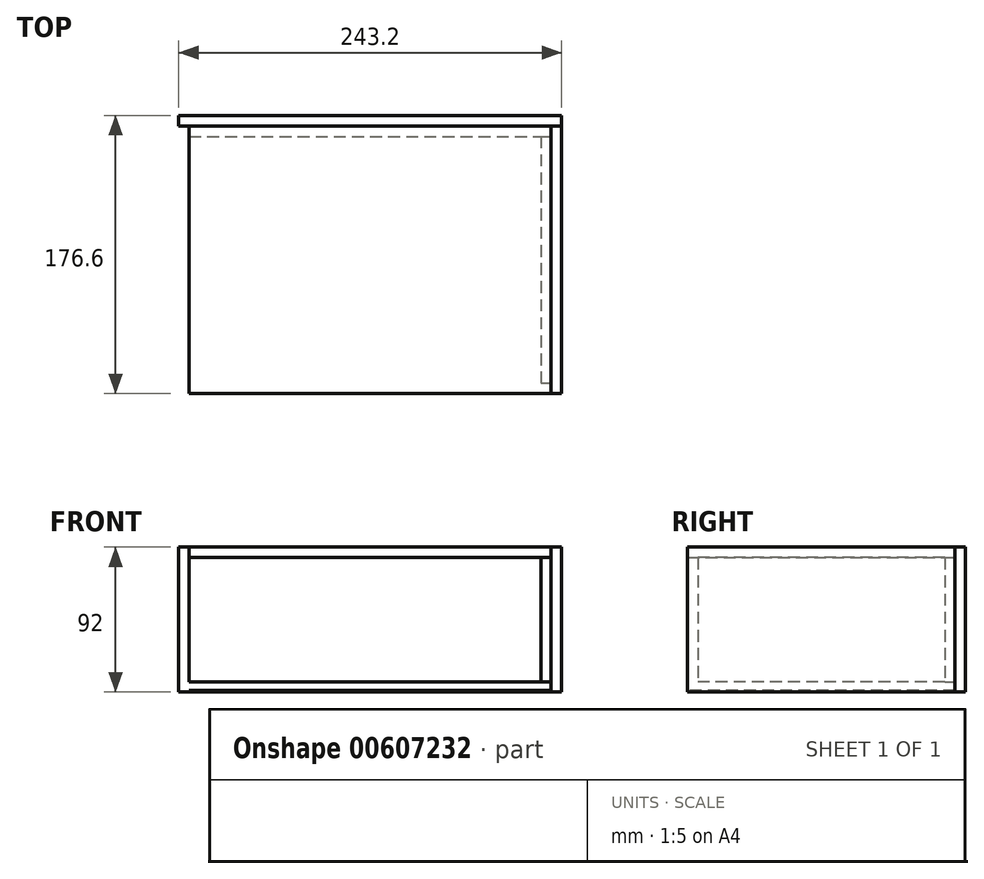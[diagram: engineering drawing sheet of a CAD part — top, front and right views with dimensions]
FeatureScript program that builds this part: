
annotation { "Feature Type Name" : "Feature", "Feature Type Description" : "" }
export const myFeature = defineFeature(function(context is Context, id is Id, definition is map)
    precondition{}
    {
        {
            var Q0;
            Q0=qCreatedBy(makeId("Top.planeOp"),FACE);
            var sketch = newSketch(context, id + "F0", { "sketchPlane" : qUnion([Q0])});
            skLineSegment(sketch, "E0.bottom", {"start": v(-115, 85) * mm, "end": v(115, 85) * mm});
            skLineSegment(sketch, "E0.top", {"start": v(-115, -85) * mm, "end": v(115, -85) * mm});
            skLineSegment(sketch, "E0.left", {"start": v(-115, 85) * mm, "end": v(-115, -85) * mm});
            skLineSegment(sketch, "E0.right", {"start": v(115, 85) * mm, "end": v(115, -85) * mm});
            skPoint(sketch, "E0.middle", {"position": v(0, 0) * mm});
            skSolve(sketch);
        }
        {
            var Q0;
            Q0 = qSketchRegion(id + "F0", true);
            extrude(context, id + "F1", {"entities" : qUnion([Q0]), "depth" : 1 * mm, "offsetDistance" : 25 * mm});
        }
        {
            var Q0;
            Q0=makeQuery(id+"F1.opExtrude","SWEPT_FACE",FACE,{"disambiguationData":[OSD([sQuery(id+"F0.wireOp",EDGE,"E0.right")])]});
            var sketch = newSketch(context, id + "F2", { "sketchPlane" : qUnion([Q0])});
            skLineSegment(sketch, "E1.bottom", {"start": v(-85, 92) * mm, "end": v(85, 92) * mm});
            skLineSegment(sketch, "E1.top", {"start": v(-85, 0) * mm, "end": v(85, 0) * mm});
            skLineSegment(sketch, "E1.left", {"start": v(-85, 92) * mm, "end": v(-85, 0) * mm});
            skLineSegment(sketch, "E1.right", {"start": v(85, 92) * mm, "end": v(85, 0) * mm});
            skSolve(sketch);
        }
        {
            var Q0;
            Q0 = qSketchRegion(id + "F2", true);
            extrude(context, id + "F3", {"entities" : qUnion([Q0]), "depth" : 6.6 * mm, "offsetDistance" : 25 * mm});
        }
        {
            var Q0;
            Q0=makeQuery(id+"F1.opExtrude","SWEPT_FACE",FACE,{"disambiguationData":[OSD([sQuery(id+"F0.wireOp",EDGE,"E0.bottom")])]});
            var sketch = newSketch(context, id + "F4", { "sketchPlane" : qUnion([Q0])});
            skLineSegment(sketch, "E2.bottom", {"start": v(-121.6, 92) * mm, "end": v(121.6, 92) * mm});
            skLineSegment(sketch, "E2.top", {"start": v(-121.6, 0) * mm, "end": v(121.6, 0) * mm});
            skLineSegment(sketch, "E2.left", {"start": v(-121.6, 92) * mm, "end": v(-121.6, 0) * mm});
            skLineSegment(sketch, "E2.right", {"start": v(121.6, 92) * mm, "end": v(121.6, 0) * mm});
            skSolve(sketch);
        }
        {
            var Q0;
            Q0 = qSketchRegion(id + "F4", true);
            extrude(context, id + "F5", {"entities" : qUnion([Q0]), "depth" : 6.6 * mm, "offsetDistance" : 25 * mm});
        }
        {
            var Q0;
            Q0=makeQuery(id+"F5.opExtrude","CAP_FACE",FACE,{"disambiguationData":[OSD([sQuery(id+"F4.wireOp",EDGE,"E2.bottom"),sQuery(id+"F4.wireOp",EDGE,"E2.top"),sQuery(id+"F4.wireOp",EDGE,"E2.left"),sQuery(id+"F4.wireOp",EDGE,"E2.right")])],"isStart":true});
            var sketch = newSketch(context, id + "F6", { "sketchPlane" : qUnion([Q0])});
            skLineSegment(sketch, "E3.bottom", {"start": v(-115, 85.4) * mm, "end": v(115, 85.4) * mm});
            skLineSegment(sketch, "E3.top", {"start": v(-115, 6.4) * mm, "end": v(115, 6.4) * mm});
            skLineSegment(sketch, "E3.left", {"start": v(-115, 85.4) * mm, "end": v(-115, 6.4) * mm});
            skLineSegment(sketch, "E3.right", {"start": v(115, 85.4) * mm, "end": v(115, 6.4) * mm});
            skSolve(sketch);
        }
        {
            var Q0;
            Q0 = qSketchRegion(id + "F6", true);
            extrude(context, id + "F7", {"entities" : qUnion([Q0]), "depth" : 6.6 * mm, "offsetDistance" : 25 * mm});
        }
        {
            var Q0;
            Q0=makeQuery(id+"F3.opExtrude","CAP_FACE",FACE,{"disambiguationData":[OSD([sQuery(id+"F2.wireOp",EDGE,"E1.bottom"),sQuery(id+"F2.wireOp",EDGE,"E1.top"),sQuery(id+"F2.wireOp",EDGE,"E1.left"),sQuery(id+"F2.wireOp",EDGE,"E1.right")])],"isStart":true});
            var sketch = newSketch(context, id + "F8", { "sketchPlane" : qUnion([Q0])});
            skLineSegment(sketch, "E4.bottom", {"start": v(-78.4, 85.4) * mm, "end": v(78.4, 85.4) * mm});
            skLineSegment(sketch, "E4.top", {"start": v(-78.4, 6.4) * mm, "end": v(78.4, 6.4) * mm});
            skLineSegment(sketch, "E4.left", {"start": v(-78.4, 85.4) * mm, "end": v(-78.4, 6.4) * mm});
            skLineSegment(sketch, "E4.right", {"start": v(78.4, 85.4) * mm, "end": v(78.4, 6.4) * mm});
            skSolve(sketch);
        }
        {
            var Q0;
            Q0 = qSketchRegion(id + "F8", true);
            var Q1;
            Q1 = qSketchRegion(id + "F10", true);
            extrude(context, id + "F9", {"entities" : qUnion([Q0, Q1]), "depth" : 6.6 * mm, "offsetDistance" : 25 * mm});
        }
        {
            var Q0;
            Q0=makeQuery(id+"F7.opExtrude","SWEPT_FACE",FACE,{"disambiguationData":[OSD([sQuery(id+"F6.wireOp",EDGE,"E3.bottom")])]});
            var sketch = newSketch(context, id + "F10", { "sketchPlane" : qUnion([Q0])});
            skLineSegment(sketch, "E5.bottom", {"start": v(-115, 85) * mm, "end": v(115, 85) * mm});
            skLineSegment(sketch, "E5.top", {"start": v(-115, -85) * mm, "end": v(115, -85) * mm});
            skLineSegment(sketch, "E5.left", {"start": v(-115, 85) * mm, "end": v(-115, -85) * mm});
            skLineSegment(sketch, "E5.right", {"start": v(115, 85) * mm, "end": v(115, -85) * mm});
            skSolve(sketch);
        }
        {
            var Q0;
            Q0 = qSketchRegion(id + "F10", true);
            extrude(context, id + "F11", {"entities" : qUnion([Q0]), "depth" : 6.6 * mm, "offsetDistance" : 25 * mm});
        }
    });
